# Revit family: Sanitary_Wash-basins_hansgrohe_60234XXX-Xanuia-Q-Handrinse-basin-500-39_NEW
name_source: partatom
category: Plumbing Fixtures
units: mm (PartAtom-declared; Revit-internal decimal feet)

## family parameters
Always vertical = No
Cut with Voids When Loaded = No
OmniClass Number = 23.31.13.00
OmniClass Title = Sinks
Part Type = Normal
Room Calculation Point = No
Round Connector Dimension = Use Diameter
Shared = No
Work Plane-Based = Yes

## types (1)
- 450 White
    Assembly Code = D2010 | Plumbing Fixtures
    Connector Description = Water Outlet 46 mm
    Default Elevation = 1219 mm
    Description = Xanuia Q Handrinse basin 500/390 without tap hole and overflow
    Diameter = 46 mm  [stored 0.150919 ft]
    ETIM Code = EC011550
    ETIM Title = Washbasin
    Edition number = 0
    Keynote = 22 41 16.13 | Residential Lavatories
    Manufacturer = Hansgrohe
    Material = Hansgrohe - Ceramic - 450 White
    Model = 60234XXX
    Product Guid = a28666c6-c523-4cba-b0eb-15d7766a45ed
    Product Page URL = https://www.hansgrohe.com
    Product data url = https://bimobject.com
    URL = https://www.hansgrohe.com
    Uniclass 2015 Code = Pr_40_20_96
    Uniclass 2015 Name = Wash basins, sinks and troughs
    Version = 1

note: [stored X ft] marks values corroborated as IEEE doubles in the binary element streams (Revit-internal decimal feet)

## geometry (parser evidence)
native form markers: Sweep x2
no freeform markers — native parametric forms only
